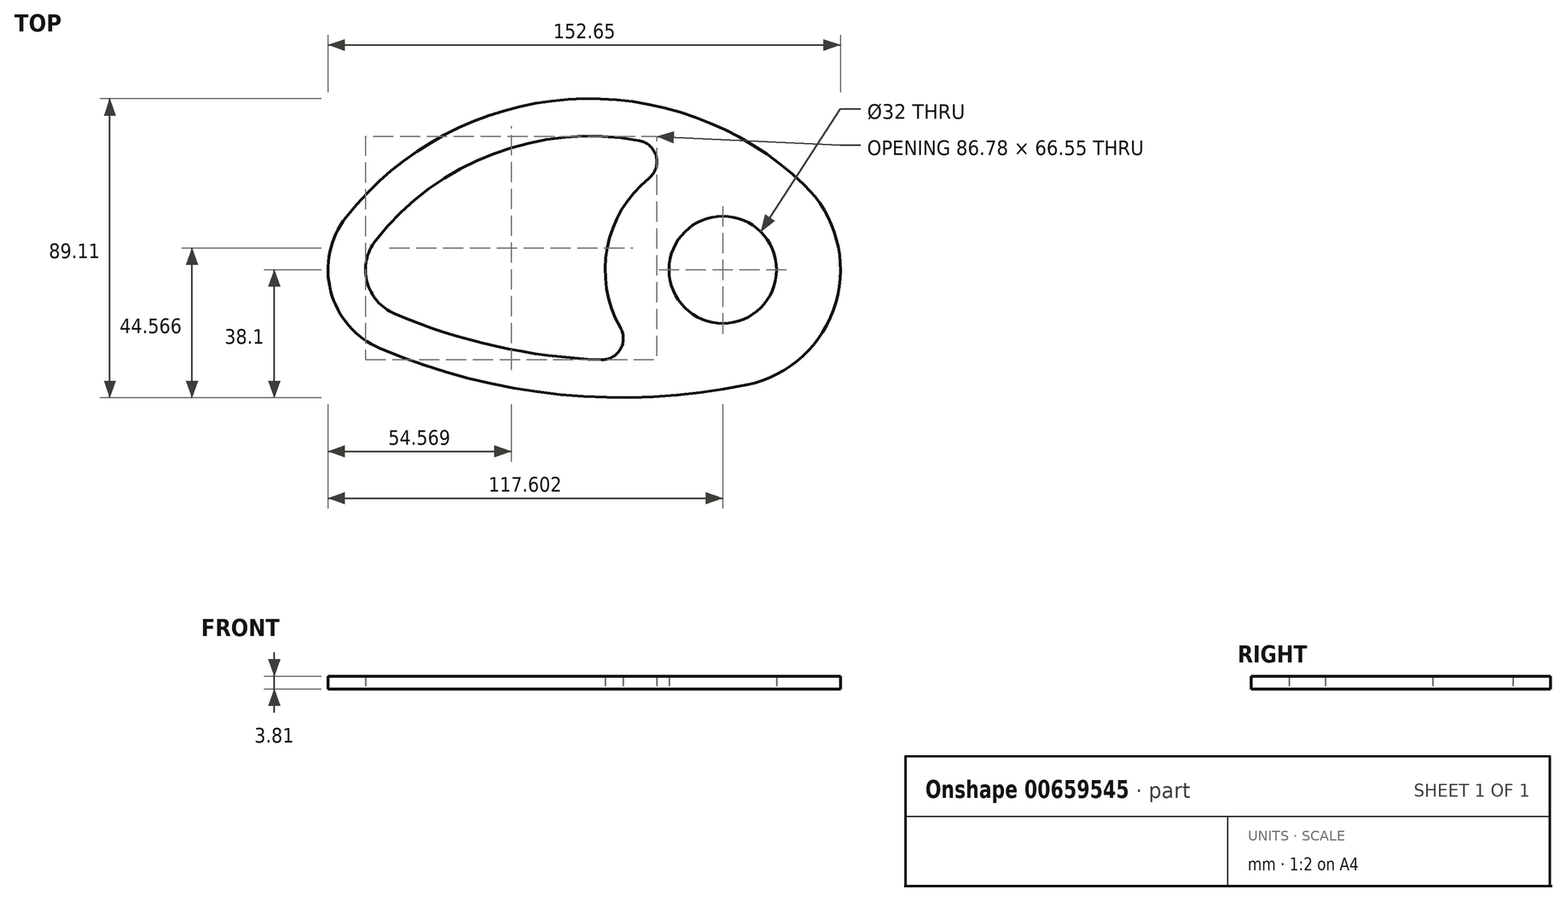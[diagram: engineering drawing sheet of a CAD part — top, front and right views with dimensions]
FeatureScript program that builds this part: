
annotation { "Feature Type Name" : "Feature", "Feature Type Description" : "" }
export const myFeature = defineFeature(function(context is Context, id is Id, definition is map)
    precondition{}
    {
        {
            var Q0;
            Q0=qCreatedBy(makeId("Top.planeOp"),FACE);
            var sketch = newSketch(context, id + "F0", { "sketchPlane" : qUnion([Q0])});
            skArc(sketch, "E0", {"start": v(-20, 15.66) * mm, "mid": v(-24.6, -6.33) * mm, "end": v(-9.95, -23.37) * mm});
            skCircle(sketch, "E1", {"center": v(92.2, 0) * mm, "radius": 16 * mm});
            skArc(sketch, "E2", {"start": v(70.2, 27.29) * mm, "mid": v(57.76, 6.54) * mm, "end": v(61.73, -17.33) * mm});
            skArc(sketch, "E3", {"start": v(116.5, 25.27) * mm, "mid": v(46.12, 50.78) * mm, "end": v(-20, 15.66) * mm});
            skArc(sketch, "E4", {"start": v(-9.95, -23.37) * mm, "mid": v(43.81, -37.18) * mm, "end": v(99.25, -34.34) * mm});
            skArc(sketch, "E5.0", {"start": v(-5.57, -13.09) * mm, "mid": v(24.57, -22.78) * mm, "end": v(55.98, -26.81) * mm});
            skArc(sketch, "E5.1", {"start": v(-11.2, 8.77) * mm, "mid": v(-13.78, -3.54) * mm, "end": v(-5.57, -13.09) * mm});
            skArc(sketch, "E5.2", {"start": v(67.37, 38.47) * mm, "mid": v(23.94, 34.6) * mm, "end": v(-11.2, 8.77) * mm});
            skArc(sketch, "E6.trimOffspring", {"start": v(99.25, -34.34) * mm, "mid": v(125.87, -9.74) * mm, "end": v(116.5, 25.27) * mm});
            skPoint(sketch, "E7.visualSharp", {"position": v(83.13, 33.86) * mm});
            skArc(sketch, "E7.filletArc", {"start": v(70.2, 27.29) * mm, "mid": v(72.37, 33.79) * mm, "end": v(67.37, 38.47) * mm});
            skPoint(sketch, "E8.visualSharp", {"position": v(69.57, -26.77) * mm});
            skArc(sketch, "E8.filletArc", {"start": v(55.98, -26.81) * mm, "mid": v(61.64, -23.76) * mm, "end": v(61.73, -17.33) * mm});
            skSolve(sketch);
        }
        {
            var Q0;
            Q0 = qSketchRegion(id + "F0", true);
            extrude(context, id + "F1", {"entities" : qUnion([Q0]), "depth" : 3.8 * mm, "offsetDistance" : 25.4 * mm});
        }
    });
